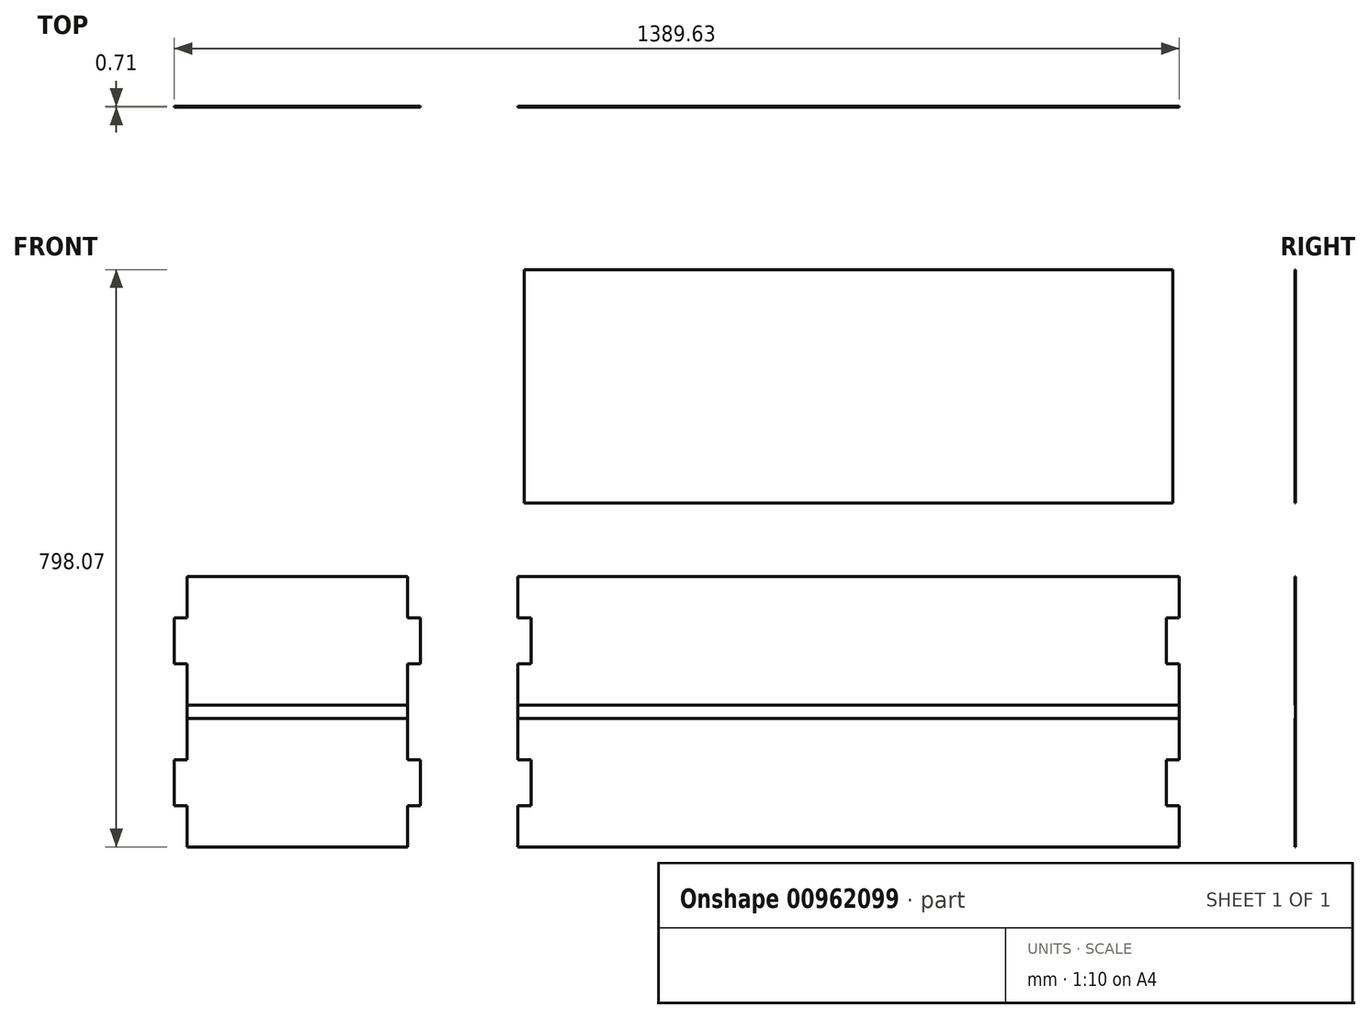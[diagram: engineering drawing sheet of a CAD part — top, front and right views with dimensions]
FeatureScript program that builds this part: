
annotation { "Feature Type Name" : "Feature", "Feature Type Description" : "" }
export const myFeature = defineFeature(function(context is Context, id is Id, definition is map)
    precondition{}
    {
        {
            assignVariable(context, id + "F0", {"name" : "ply34", "anyValue" : .71});
        }
        {
            var Q0;
            Q0=qCreatedBy(makeId("Front.planeOp"),FACE);
            var sketch = newSketch(context, id + "F1", { "sketchPlane" : qUnion([Q0])});
            skLineSegment(sketch, "E0.bottom", {"start": v(-457.2, 186.82) * mm, "end": v(457.2, 186.82) * mm});
            skLineSegment(sketch, "E0.top", {"start": v(-457.2, -186.82) * mm, "end": v(457.2, -186.82) * mm});
            skLineSegment(sketch, "E0.left", {"start": v(-457.2, 186.82) * mm, "end": v(-457.2, -186.82) * mm});
            skLineSegment(sketch, "E0.right", {"start": v(457.2, 186.82) * mm, "end": v(457.2, -186.82) * mm});
            skPoint(sketch, "E0.middle", {"position": v(0, 0) * mm});
            skLineSegment(sketch, "E1.bottom", {"start": v(-609.6, 186.82) * mm, "end": v(-914.4, 186.82) * mm});
            skLineSegment(sketch, "E1.top", {"start": v(-609.6, -186.82) * mm, "end": v(-914.4, -186.82) * mm});
            skLineSegment(sketch, "E1.left", {"start": v(-609.6, 186.82) * mm, "end": v(-609.6, -186.82) * mm});
            skLineSegment(sketch, "E1.right", {"start": v(-914.4, 186.82) * mm, "end": v(-914.4, -186.82) * mm});
            skLineSegment(sketch, "E2.bottom", {"start": v(-609.6, 129.67) * mm, "end": v(-591.57, 129.67) * mm});
            skLineSegment(sketch, "E2.top", {"start": v(-609.6, 66.17) * mm, "end": v(-591.57, 66.17) * mm});
            skLineSegment(sketch, "E2.left", {"start": v(-609.6, 129.67) * mm, "end": v(-609.6, 66.17) * mm});
            skLineSegment(sketch, "E2.right", {"start": v(-591.57, 129.67) * mm, "end": v(-591.57, 66.17) * mm});
            skLineSegment(sketch, "E3", {"start": v(-457.2, 0) * mm, "end": v(-609.6, 0) * mm, "construction": true});
            skLineSegment(sketch, "E4.MirrorCS", {"start": v(-609.6, -129.67) * mm, "end": v(-591.57, -129.67) * mm});
            skLineSegment(sketch, "E5.MirrorCS", {"start": v(-609.6, -66.17) * mm, "end": v(-591.57, -66.17) * mm});
            skLineSegment(sketch, "E6.MirrorCS", {"start": v(-609.6, -129.67) * mm, "end": v(-609.6, -66.17) * mm});
            skLineSegment(sketch, "E7.MirrorCS", {"start": v(-591.57, -129.67) * mm, "end": v(-591.57, -66.17) * mm});
            skLineSegment(sketch, "E8", {"start": v(-591.57, 97.92) * mm, "end": v(-457.2, 97.92) * mm, "construction": true});
            skLineSegment(sketch, "E9", {"start": v(-524.38, 97.92) * mm, "end": v(-524.38, 0) * mm, "construction": true});
            skLineSegment(sketch, "E10.MirrorCS", {"start": v(-439.17, 129.67) * mm, "end": v(-457.2, 129.67) * mm});
            skLineSegment(sketch, "E11.MirrorCS", {"start": v(-439.17, -129.67) * mm, "end": v(-457.2, -129.67) * mm});
            skLineSegment(sketch, "E12.MirrorCS", {"start": v(-439.17, 66.17) * mm, "end": v(-457.2, 66.17) * mm});
            skLineSegment(sketch, "E13.MirrorCS", {"start": v(-439.17, -66.17) * mm, "end": v(-457.2, -66.17) * mm});
            skLineSegment(sketch, "E14.MirrorCS", {"start": v(-439.17, 129.67) * mm, "end": v(-439.17, 66.17) * mm});
            skLineSegment(sketch, "E15.MirrorCS", {"start": v(-457.2, -129.67) * mm, "end": v(-457.2, -66.17) * mm});
            skLineSegment(sketch, "E16.MirrorCS", {"start": v(-457.2, 129.67) * mm, "end": v(-457.2, 66.17) * mm});
            skLineSegment(sketch, "E17.MirrorCS", {"start": v(-439.17, -129.67) * mm, "end": v(-439.17, -66.17) * mm});
            skLineSegment(sketch, "E18", {"start": v(-762, 186.82) * mm, "end": v(-762, -186.82) * mm, "construction": true});
            skLineSegment(sketch, "E19", {"start": v(0, 186.82) * mm, "end": v(0, -186.82) * mm, "construction": true});
            skLineSegment(sketch, "E20.MirrorCS", {"start": v(-932.43, 129.67) * mm, "end": v(-932.43, 66.17) * mm});
            skLineSegment(sketch, "E21.MirrorCS", {"start": v(-914.4, 66.17) * mm, "end": v(-932.43, 66.17) * mm});
            skLineSegment(sketch, "E22.MirrorCS", {"start": v(-914.4, -129.67) * mm, "end": v(-932.43, -129.67) * mm});
            skLineSegment(sketch, "E23.MirrorCS", {"start": v(-914.4, -66.17) * mm, "end": v(-932.43, -66.17) * mm});
            skLineSegment(sketch, "E24.MirrorCS", {"start": v(-914.4, 129.67) * mm, "end": v(-932.43, 129.67) * mm});
            skLineSegment(sketch, "E25.MirrorCS", {"start": v(-914.4, 129.67) * mm, "end": v(-914.4, 66.17) * mm});
            skLineSegment(sketch, "E26.MirrorCS", {"start": v(-932.43, -129.67) * mm, "end": v(-932.43, -66.17) * mm});
            skLineSegment(sketch, "E27.MirrorCS", {"start": v(-914.4, -129.67) * mm, "end": v(-914.4, -66.17) * mm});
            skLineSegment(sketch, "E28.MirrorCS", {"start": v(439.17, -66.17) * mm, "end": v(457.2, -66.17) * mm});
            skLineSegment(sketch, "E29.MirrorCS", {"start": v(439.17, -129.67) * mm, "end": v(457.2, -129.67) * mm});
            skLineSegment(sketch, "E30.MirrorCS", {"start": v(439.17, 66.17) * mm, "end": v(457.2, 66.17) * mm});
            skLineSegment(sketch, "E31.MirrorCS", {"start": v(439.17, 129.67) * mm, "end": v(457.2, 129.67) * mm});
            skLineSegment(sketch, "E32.MirrorCS", {"start": v(457.2, 129.67) * mm, "end": v(457.2, 66.17) * mm});
            skLineSegment(sketch, "E33.MirrorCS", {"start": v(457.2, -129.67) * mm, "end": v(457.2, -66.17) * mm});
            skLineSegment(sketch, "E34.MirrorCS", {"start": v(439.17, -129.67) * mm, "end": v(439.17, -66.17) * mm});
            skLineSegment(sketch, "E35.MirrorCS", {"start": v(439.17, 129.67) * mm, "end": v(439.17, 66.17) * mm});
            skPoint(sketch, "E36.firstSnap0", {"position": v(-448.18, 129.67) * mm});
            skPoint(sketch, "E36.oppositeSnap0", {"position": v(448.18, 129.67) * mm});
            skLineSegment(sketch, "E36.bottom", {"start": v(-448.18, 611.25) * mm, "end": v(448.18, 611.25) * mm});
            skLineSegment(sketch, "E36.top", {"start": v(-448.18, 288.42) * mm, "end": v(448.18, 288.42) * mm});
            skLineSegment(sketch, "E36.left", {"start": v(-448.18, 611.25) * mm, "end": v(-448.18, 288.42) * mm});
            skLineSegment(sketch, "E36.right", {"start": v(448.18, 611.25) * mm, "end": v(448.18, 288.42) * mm});
            skLineSegment(sketch, "E37.bottom", {"start": v(-609.6, 9.02) * mm, "end": v(-914.4, 9.02) * mm});
            skLineSegment(sketch, "E37.top", {"start": v(-609.6, -9.02) * mm, "end": v(-914.4, -9.02) * mm});
            skLineSegment(sketch, "E37.left", {"start": v(-609.6, 9.02) * mm, "end": v(-609.6, -9.02) * mm});
            skLineSegment(sketch, "E37.right", {"start": v(-914.4, 9.02) * mm, "end": v(-914.4, -9.02) * mm});
            skPoint(sketch, "E37.middle", {"position": v(-762, 0) * mm});
            skLineSegment(sketch, "E38.bottom", {"start": v(-457.2, 9.02) * mm, "end": v(457.2, 9.02) * mm});
            skLineSegment(sketch, "E38.top", {"start": v(-457.2, -9.02) * mm, "end": v(457.2, -9.02) * mm});
            skLineSegment(sketch, "E38.left", {"start": v(-457.2, 9.02) * mm, "end": v(-457.2, -9.02) * mm});
            skLineSegment(sketch, "E38.right", {"start": v(457.2, 9.02) * mm, "end": v(457.2, -9.02) * mm});
            skSolve(sketch);
        }
        {
            var Q0;
            {var subQ1=sQuery(id+"F1.wireOp",EDGE,"E1.bottom");Q0=makeQuery(id+"F1.imprint","IMPRINT",FACE,{"disambiguationData":[TD([[makeQuery(id+"F1.imprint","IMPRINT",EDGE,{"derivedFrom":subQ1}),1.0]])]});}
            var Q1;
            Q1=makeQuery(id+"F1.imprint","IMPRINT",FACE,{"disambiguationData":[TD([[makeQuery(id+"F1.imprint","IMPRINT",EDGE,{"derivedFrom":sQuery(id+"F1.wireOp",EDGE,"E20.MirrorCS")}),1.0]])]});
            var Q2;
            {var subQ2=sQuery(id+"F1.wireOp",EDGE,"E22.MirrorCS");Q2=makeQuery(id+"F1.imprint","IMPRINT",FACE,{"disambiguationData":[TD([[makeQuery(id+"F1.imprint","IMPRINT",EDGE,{"derivedFrom":subQ2}),-1.0]])]});}
            var Q3;
            {var subQ0=sQuery(id+"F1.wireOp",EDGE,"E2.bottom");Q3=makeQuery(id+"F1.imprint","IMPRINT",FACE,{"disambiguationData":[TD([[makeQuery(id+"F1.imprint","IMPRINT",EDGE,{"derivedFrom":subQ0}),-1.0]])]});}
            var Q4;
            {var subQ0=sQuery(id+"F1.wireOp",EDGE,"E4.MirrorCS");Q4=makeQuery(id+"F1.imprint","IMPRINT",FACE,{"disambiguationData":[TD([[makeQuery(id+"F1.imprint","IMPRINT",EDGE,{"derivedFrom":subQ0}),1.0]])]});}
            var Q5;
            {var subQ5=sQuery(id+"F1.wireOp",EDGE,"E0.top");Q5=makeQuery(id+"F1.imprint","IMPRINT",FACE,{"disambiguationData":[TD([[makeQuery(id+"F1.imprint","IMPRINT",EDGE,{"derivedFrom":subQ5}),1.0]])]});}
            var Q6;
            {var subQ18=sQuery(id+"F1.wireOp",EDGE,"4i3ZQTJm-VDd4-fkp7-lnd4-wDdlG6TSANmu.bottom");Q6=makeQuery(id+"F1.imprint","IMPRINT",FACE,{"disambiguationData":[TD([[makeQuery(id+"F1.imprint","IMPRINT",EDGE,{"derivedFrom":subQ18}),1.0]])]});}
            var Q7;
            {var subQ0=sQuery(id+"F1.wireOp",EDGE,"7c33b191-6131-4162-a389-dcece145f6040.MirrorCS");Q7=makeQuery(id+"F1.imprint","IMPRINT",FACE,{"disambiguationData":[TD([[makeQuery(id+"F1.imprint","IMPRINT",EDGE,{"derivedFrom":subQ0}),1.0]])]});}
            var Q8;
            {var subQ0=sQuery(id+"F1.wireOp",EDGE,"7c33b191-6131-4162-a389-dcece145f6041.MirrorCS");Q8=makeQuery(id+"F1.imprint","IMPRINT",FACE,{"disambiguationData":[TD([[makeQuery(id+"F1.imprint","IMPRINT",EDGE,{"derivedFrom":subQ0}),-1.0]])]});}
            var Q9;
            {var subQ0=sQuery(id+"F1.wireOp",EDGE,"51cc2190-801a-4cf8-9ff8-84556132d8cd0.MirrorCS");Q9=makeQuery(id+"F1.imprint","IMPRINT",FACE,{"disambiguationData":[TD([[makeQuery(id+"F1.imprint","IMPRINT",EDGE,{"derivedFrom":subQ0}),1.0]])]});}
            var Q10;
            Q10=makeQuery(id+"F1.imprint","IMPRINT",FACE,{"disambiguationData":[TD([[makeQuery(id+"F1.imprint","IMPRINT",EDGE,{"derivedFrom":sQuery(id+"F1.wireOp",EDGE,"gPGnPhEg-uLDh-ps2B-oY2R-4i2IYrPyc44U.top")}),1.0]])]});
            var Q11;
            {var subQ16=sQuery(id+"F1.wireOp",EDGE,"4i3ZQTJm-VDd4-fkp7-lnd4-wDdlG6TSANmu.left");Q11=makeQuery(id+"F1.imprint","IMPRINT",FACE,{"disambiguationData":[TD([[makeQuery(id+"F1.imprint","IMPRINT",EDGE,{"derivedFrom":subQ16}),1.0]])]});}
            var Q12;
            Q12=makeQuery(id+"F1.imprint","IMPRINT",FACE,{"disambiguationData":[TD([[makeQuery(id+"F1.imprint","IMPRINT",EDGE,{"derivedFrom":sQuery(id+"F1.wireOp",EDGE,"4i3ZQTJm-VDd4-fkp7-lnd4-wDdlG6TSANmu.left")}),-1.0]])]});
            var Q13;
            Q13=makeQuery(id+"F1.imprint","IMPRINT",FACE,{"disambiguationData":[TD([[makeQuery(id+"F1.imprint","IMPRINT",EDGE,{"derivedFrom":sQuery(id+"F1.wireOp",EDGE,"29be0488-762e-4d2c-ba13-169632d951932.MirrorCS")}),1.0]])]});
            var Q14;
            {var subQ1=sQuery(id+"F1.wireOp",EDGE,"E1.top");Q14=makeQuery(id+"F1.imprint","IMPRINT",FACE,{"disambiguationData":[TD([[makeQuery(id+"F1.imprint","IMPRINT",EDGE,{"derivedFrom":subQ1}),-1.0]])]});}
            var Q15;
            {var subQ7=sQuery(id+"F1.wireOp",EDGE,"E0.bottom");Q15=makeQuery(id+"F1.imprint","IMPRINT",FACE,{"disambiguationData":[TD([[makeQuery(id+"F1.imprint","IMPRINT",EDGE,{"derivedFrom":subQ7}),-1.0]])]});}
            var Q16;
            Q16=makeQuery(id+"F1.imprint","IMPRINT",FACE,{"disambiguationData":[TD([[makeQuery(id+"F1.imprint","IMPRINT",EDGE,{"derivedFrom":sQuery(id+"F1.wireOp",EDGE,"E36.bottom")}),-1.0]])]});
            extrude(context, id + "F2", {"entities" : qUnion([Q0, Q1, Q2, Q3, Q4, Q5, Q6, Q7, Q8, Q9, Q10, Q11, Q12, Q13, Q14, Q15, Q16]), "depth" : (getVariable(context, 'ply34')) * mm, "offsetDistance" : 25.4 * mm});
        }
        {
            var Q0;
            {var subQ2=sQuery(id+"F1.wireOp",EDGE,"E37.bottom");Q0=makeQuery(id+"F1.imprint","IMPRINT",FACE,{"disambiguationData":[TD([[makeQuery(id+"F1.imprint","IMPRINT",EDGE,{"derivedFrom":subQ2}),1.0]])]});}
            var Q1;
            {var subQ2=sQuery(id+"F1.wireOp",EDGE,"E38.bottom");Q1=makeQuery(id+"F1.imprint","IMPRINT",FACE,{"disambiguationData":[TD([[makeQuery(id+"F1.imprint","IMPRINT",EDGE,{"derivedFrom":subQ2}),-1.0]])]});}
            extrude(context, id + "F3", {"entities" : qUnion([Q0, Q1]), "operationType" : NewBodyOperationType.ADD, "depth" : (getVariable(context, 'ply34') / 2) * mm, "offsetDistance" : 25.4 * mm});
        }
    });
